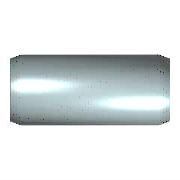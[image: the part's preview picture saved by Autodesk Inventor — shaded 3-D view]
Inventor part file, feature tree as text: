
AUTODESK INVENTOR PART (.ipt)
format: ipt  version: 2023.3 (Build 273359000, 359)  size: 113,152 bytes
history: native  units: mm (DEFAULTED — no unit token found)
features: extrude x1, chamfer x1, sketch x1
ambient origin geometry x8: Origin, YZ Plane, XZ Plane, XY Plane, X Axis, Y Axis, Z Axis, Center Point
bodies: Solid1 (feature_tree)
feature tree (3):
  extrude  "Körper"  Depth=24.0mm
  chamfer  "Skizze2"  [1 undecoded]
  sketch  "Skizze"  dims[d1=2.0mm d2=24.0mm d3=0.0mm d4=0.35mm d5=15.0deg d8=0.35mm d9=15.0deg d11=0.35mm d12=0.35mm d13=0.0mm d15=0.0mm d16=0.0mm]
note: 1 required parameter value undecoded (feature->parameter linkage not recoverable at this tier; creation-order binding heuristic only, values carry confidence <= 0.55)
